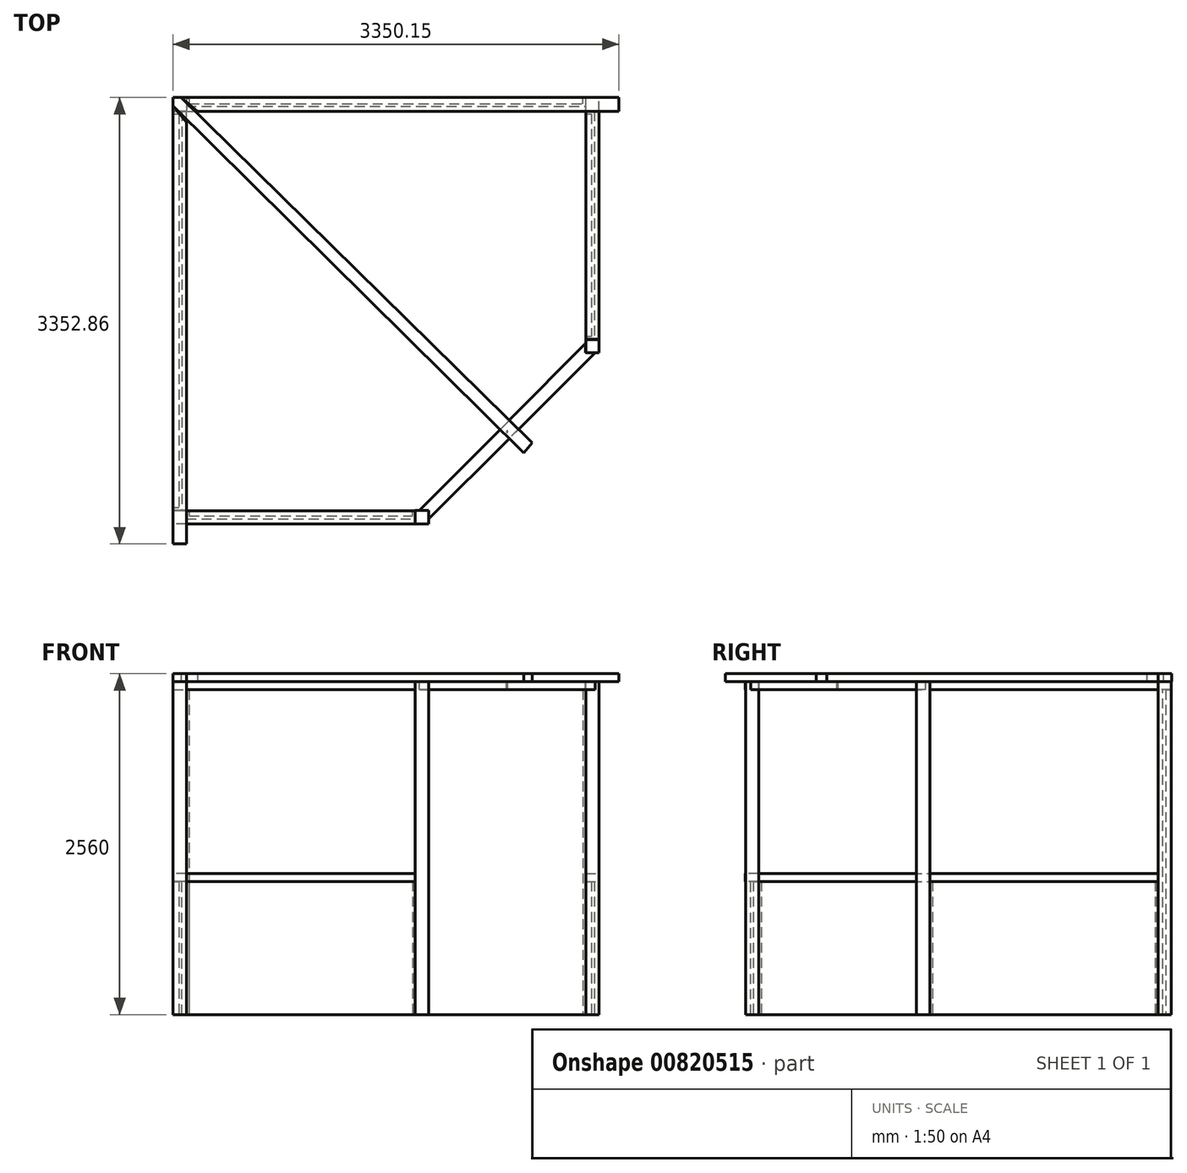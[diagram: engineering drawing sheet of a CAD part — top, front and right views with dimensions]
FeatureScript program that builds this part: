
annotation { "Feature Type Name" : "Feature", "Feature Type Description" : "" }
export const myFeature = defineFeature(function(context is Context, id is Id, definition is map)
    precondition{}
    {
        {
            var Q0;
            Q0=qCreatedBy(makeId("Top.planeOp"),FACE);
            var sketch = newSketch(context, id + "F0", { "sketchPlane" : qUnion([Q0])});
            skLineSegment(sketch, "E0.bottom", {"start": v(-213.47, 1424.3) * mm, "end": v(-113.47, 1424.3) * mm});
            skLineSegment(sketch, "E0.top", {"start": v(-213.47, 1324.3) * mm, "end": v(-113.47, 1324.3) * mm});
            skLineSegment(sketch, "E0.left", {"start": v(-213.47, 1424.3) * mm, "end": v(-213.47, 1324.3) * mm});
            skLineSegment(sketch, "E0.right", {"start": v(-113.47, 1424.3) * mm, "end": v(-113.47, 1324.3) * mm});
            skLineSegment(sketch, "E1.bottom", {"start": v(2886.53, 1324.3) * mm, "end": v(2986.53, 1324.3) * mm});
            skLineSegment(sketch, "E1.top", {"start": v(2886.53, 1424.3) * mm, "end": v(2986.53, 1424.3) * mm});
            skLineSegment(sketch, "E1.left", {"start": v(2886.53, 1324.3) * mm, "end": v(2886.53, 1424.3) * mm});
            skLineSegment(sketch, "E1.right", {"start": v(2986.53, 1324.3) * mm, "end": v(2986.53, 1424.3) * mm});
            skLineSegment(sketch, "E2.bottom", {"start": v(-113.47, -1675.7) * mm, "end": v(-213.47, -1675.7) * mm});
            skLineSegment(sketch, "E2.top", {"start": v(-113.47, -1775.7) * mm, "end": v(-213.47, -1775.7) * mm});
            skLineSegment(sketch, "E2.left", {"start": v(-113.47, -1675.7) * mm, "end": v(-113.47, -1775.7) * mm});
            skLineSegment(sketch, "E2.right", {"start": v(-213.47, -1675.7) * mm, "end": v(-213.47, -1775.7) * mm});
            skLineSegment(sketch, "E3.bottom", {"start": v(1606.53, -1675.7) * mm, "end": v(1706.53, -1675.7) * mm});
            skLineSegment(sketch, "E3.top", {"start": v(1606.53, -1775.7) * mm, "end": v(1706.53, -1775.7) * mm});
            skLineSegment(sketch, "E3.left", {"start": v(1606.53, -1675.7) * mm, "end": v(1606.53, -1775.7) * mm});
            skLineSegment(sketch, "E3.right", {"start": v(1706.53, -1675.7) * mm, "end": v(1706.53, -1775.7) * mm});
            skLineSegment(sketch, "E4.bottom", {"start": v(2886.53, -390.7) * mm, "end": v(2986.53, -390.7) * mm});
            skLineSegment(sketch, "E4.top", {"start": v(2886.53, -490.7) * mm, "end": v(2986.53, -490.7) * mm});
            skLineSegment(sketch, "E4.left", {"start": v(2886.53, -390.7) * mm, "end": v(2886.53, -490.7) * mm});
            skLineSegment(sketch, "E4.right", {"start": v(2986.53, -390.7) * mm, "end": v(2986.53, -490.7) * mm});
            skSolve(sketch);
        }
        {
            var Q0;
            Q0 = qSketchRegion(id + "F0", true);
            extrude(context, id + "F1", {"entities" : qUnion([Q0]), "depth" : 2500 * mm, "offsetDistance" : 25 * mm});
        }
        {
            var Q0;
            Q0=qCreatedBy(makeId("Top.planeOp"),FACE);
            var sketch = newSketch(context, id + "F2", { "sketchPlane" : qUnion([Q0])});
            skLineSegment(sketch, "E5.bottom", {"start": v(-113.6, 1421.35) * mm, "end": v(-93.6, 1421.35) * mm});
            skLineSegment(sketch, "E5.top", {"start": v(-113.6, 1381.35) * mm, "end": v(-93.6, 1381.35) * mm});
            skLineSegment(sketch, "E5.left", {"start": v(-113.6, 1421.35) * mm, "end": v(-113.6, 1381.35) * mm});
            skLineSegment(sketch, "E5.right", {"start": v(-93.6, 1421.35) * mm, "end": v(-93.6, 1381.35) * mm});
            skLineSegment(sketch, "E6.bottom", {"start": v(-113.6, 1381.35) * mm, "end": v(2886.4, 1381.35) * mm});
            skLineSegment(sketch, "E6.top", {"start": v(-113.6, 1360.35) * mm, "end": v(2886.4, 1360.35) * mm});
            skLineSegment(sketch, "E6.left", {"start": v(-113.6, 1381.35) * mm, "end": v(-113.6, 1360.35) * mm});
            skLineSegment(sketch, "E6.right", {"start": v(2886.4, 1381.35) * mm, "end": v(2886.4, 1360.35) * mm});
            skLineSegment(sketch, "E7.bottom", {"start": v(2886.4, 1381.35) * mm, "end": v(2866.4, 1381.35) * mm});
            skLineSegment(sketch, "E7.top", {"start": v(2886.4, 1421.35) * mm, "end": v(2866.4, 1421.35) * mm});
            skLineSegment(sketch, "E7.left", {"start": v(2886.4, 1381.35) * mm, "end": v(2886.4, 1421.35) * mm});
            skLineSegment(sketch, "E7.right", {"start": v(2866.4, 1381.35) * mm, "end": v(2866.4, 1421.35) * mm});
            skSolve(sketch);
        }
        {
            var Q0;
            Q0 = qSketchRegion(id + "F2", true);
            extrude(context, id + "F3", {"entities" : qUnion([Q0]), "operationType" : NewBodyOperationType.ADD, "depth" : 2440 * mm, "offsetDistance" : 25 * mm});
        }
        {
            var Q0;
            Q0=qCreatedBy(makeId("Top.planeOp"),FACE);
            var sketch = newSketch(context, id + "F4", { "sketchPlane" : qUnion([Q0])});
            skLineSegment(sketch, "E8.bottom", {"start": v(-209.79, 1323.87) * mm, "end": v(-169.79, 1323.87) * mm});
            skLineSegment(sketch, "E8.top", {"start": v(-209.79, 1303.87) * mm, "end": v(-169.79, 1303.87) * mm});
            skLineSegment(sketch, "E8.left", {"start": v(-209.79, 1323.87) * mm, "end": v(-209.79, 1303.87) * mm});
            skLineSegment(sketch, "E8.right", {"start": v(-169.79, 1323.87) * mm, "end": v(-169.79, 1303.87) * mm});
            skLineSegment(sketch, "E9.bottom", {"start": v(-169.79, 1323.87) * mm, "end": v(-148.79, 1323.87) * mm});
            skLineSegment(sketch, "E9.top", {"start": v(-169.79, -1676.13) * mm, "end": v(-148.79, -1676.13) * mm});
            skLineSegment(sketch, "E9.left", {"start": v(-169.79, 1323.87) * mm, "end": v(-169.79, -1676.13) * mm});
            skLineSegment(sketch, "E9.right", {"start": v(-148.79, 1323.87) * mm, "end": v(-148.79, -1676.13) * mm});
            skLineSegment(sketch, "E10.bottom", {"start": v(-169.79, -1676.13) * mm, "end": v(-209.79, -1676.13) * mm});
            skLineSegment(sketch, "E10.top", {"start": v(-169.79, -1656.13) * mm, "end": v(-209.79, -1656.13) * mm});
            skLineSegment(sketch, "E10.left", {"start": v(-169.79, -1676.13) * mm, "end": v(-169.79, -1656.13) * mm});
            skLineSegment(sketch, "E10.right", {"start": v(-209.79, -1676.13) * mm, "end": v(-209.79, -1656.13) * mm});
            skSolve(sketch);
        }
        {
            var Q0;
            Q0 = qSketchRegion(id + "F4", true);
            extrude(context, id + "F5", {"entities" : qUnion([Q0]), "operationType" : NewBodyOperationType.ADD, "depth" : 1000 * mm, "offsetDistance" : 25 * mm});
        }
        {
            var Q0;
            Q0=qCreatedBy(makeId("Top.planeOp"),FACE);
            var sketch = newSketch(context, id + "F6", { "sketchPlane" : qUnion([Q0])});
            skLineSegment(sketch, "E11.bottom", {"start": v(-113.7, -1676.3) * mm, "end": v(-93.7, -1676.3) * mm});
            skLineSegment(sketch, "E11.top", {"start": v(-113.7, -1716.3) * mm, "end": v(-93.7, -1716.3) * mm});
            skLineSegment(sketch, "E11.left", {"start": v(-113.7, -1676.3) * mm, "end": v(-113.7, -1716.3) * mm});
            skLineSegment(sketch, "E11.right", {"start": v(-93.7, -1676.3) * mm, "end": v(-93.7, -1716.3) * mm});
            skLineSegment(sketch, "E12.bottom", {"start": v(-113.7, -1716.3) * mm, "end": v(1606.3, -1716.3) * mm});
            skLineSegment(sketch, "E12.top", {"start": v(-113.7, -1737.3) * mm, "end": v(1606.3, -1737.3) * mm});
            skLineSegment(sketch, "E12.left", {"start": v(-113.7, -1716.3) * mm, "end": v(-113.7, -1737.3) * mm});
            skLineSegment(sketch, "E12.right", {"start": v(1606.3, -1716.3) * mm, "end": v(1606.3, -1737.3) * mm});
            skLineSegment(sketch, "E13.bottom", {"start": v(1606.3, -1716.3) * mm, "end": v(1586.3, -1716.3) * mm});
            skLineSegment(sketch, "E13.top", {"start": v(1606.3, -1676.3) * mm, "end": v(1586.3, -1676.3) * mm});
            skLineSegment(sketch, "E13.left", {"start": v(1606.3, -1716.3) * mm, "end": v(1606.3, -1676.3) * mm});
            skLineSegment(sketch, "E13.right", {"start": v(1586.3, -1716.3) * mm, "end": v(1586.3, -1676.3) * mm});
            skSolve(sketch);
        }
        {
            var Q0;
            Q0 = qSketchRegion(id + "F6", true);
            extrude(context, id + "F7", {"entities" : qUnion([Q0]), "operationType" : NewBodyOperationType.ADD, "depth" : 1000 * mm, "offsetDistance" : 25 * mm});
        }
        {
            var Q0;
            Q0=qCreatedBy(makeId("Top.planeOp"),FACE);
            var sketch = newSketch(context, id + "F8", { "sketchPlane" : qUnion([Q0])});
            skLineSegment(sketch, "E14.bottom", {"start": v(2889.5, 1324.2) * mm, "end": v(2929.5, 1324.2) * mm});
            skLineSegment(sketch, "E14.top", {"start": v(2889.5, 1304.2) * mm, "end": v(2929.5, 1304.2) * mm});
            skLineSegment(sketch, "E14.left", {"start": v(2889.5, 1324.2) * mm, "end": v(2889.5, 1304.2) * mm});
            skLineSegment(sketch, "E14.right", {"start": v(2929.5, 1324.2) * mm, "end": v(2929.5, 1304.2) * mm});
            skLineSegment(sketch, "E15.bottom", {"start": v(2929.5, 1324.2) * mm, "end": v(2950.5, 1324.2) * mm});
            skLineSegment(sketch, "E15.top", {"start": v(2929.5, -390.8) * mm, "end": v(2950.5, -390.8) * mm});
            skLineSegment(sketch, "E15.left", {"start": v(2929.5, 1324.2) * mm, "end": v(2929.5, -390.8) * mm});
            skLineSegment(sketch, "E15.right", {"start": v(2950.5, 1324.2) * mm, "end": v(2950.5, -390.8) * mm});
            skLineSegment(sketch, "E16.bottom", {"start": v(2929.5, -390.8) * mm, "end": v(2889.5, -390.8) * mm});
            skLineSegment(sketch, "E16.top", {"start": v(2929.5, -370.8) * mm, "end": v(2889.5, -370.8) * mm});
            skLineSegment(sketch, "E16.left", {"start": v(2929.5, -390.8) * mm, "end": v(2929.5, -370.8) * mm});
            skLineSegment(sketch, "E16.right", {"start": v(2889.5, -390.8) * mm, "end": v(2889.5, -370.8) * mm});
            skSolve(sketch);
        }
        {
            var Q0;
            Q0 = qSketchRegion(id + "F8", true);
            extrude(context, id + "F9", {"entities" : qUnion([Q0]), "operationType" : NewBodyOperationType.ADD, "depth" : 1000 * mm, "offsetDistance" : 25 * mm});
        }
        {
            var Q0;
            Q0=makeQuery(id+"F1.opExtrude","CAP_FACE",FACE,{"disambiguationData":[OSD([sQuery(id+"F0.wireOp",EDGE,"E0.bottom"),sQuery(id+"F0.wireOp",EDGE,"E0.top"),sQuery(id+"F0.wireOp",EDGE,"E0.left"),sQuery(id+"F0.wireOp",EDGE,"E0.right")])],"isStart":false});
            var sketch = newSketch(context, id + "F10", { "sketchPlane" : qUnion([Q0])});
            skLineSegment(sketch, "E17.bottom", {"start": v(-113.47, 1324.3) * mm, "end": v(2886.53, 1324.3) * mm});
            skLineSegment(sketch, "E17.top", {"start": v(-113.47, 1424.3) * mm, "end": v(2886.53, 1424.3) * mm});
            skLineSegment(sketch, "E17.left", {"start": v(-113.47, 1324.3) * mm, "end": v(-113.47, 1424.3) * mm});
            skLineSegment(sketch, "E17.right", {"start": v(2886.53, 1324.3) * mm, "end": v(2886.53, 1424.3) * mm});
            skLineSegment(sketch, "E18.bottom", {"start": v(-213.62, -1674.97) * mm, "end": v(-113.62, -1674.97) * mm});
            skLineSegment(sketch, "E18.top", {"start": v(-213.62, 1325.03) * mm, "end": v(-113.62, 1325.03) * mm});
            skLineSegment(sketch, "E18.left", {"start": v(-213.62, -1674.97) * mm, "end": v(-213.62, 1325.03) * mm});
            skLineSegment(sketch, "E18.right", {"start": v(-113.62, -1674.97) * mm, "end": v(-113.62, 1325.03) * mm});
            skLineSegment(sketch, "E19.bottom", {"start": v(-113.62, -1776.28) * mm, "end": v(1606.38, -1776.28) * mm});
            skLineSegment(sketch, "E19.top", {"start": v(-113.62, -1676.28) * mm, "end": v(1606.38, -1676.28) * mm});
            skLineSegment(sketch, "E19.left", {"start": v(-113.62, -1776.28) * mm, "end": v(-113.62, -1676.28) * mm});
            skLineSegment(sketch, "E19.right", {"start": v(1606.38, -1776.28) * mm, "end": v(1606.38, -1676.28) * mm});
            skLineSegment(sketch, "E20.bottom", {"start": v(2886.7, -389.73) * mm, "end": v(2986.7, -389.73) * mm});
            skLineSegment(sketch, "E20.top", {"start": v(2886.7, 1325.27) * mm, "end": v(2986.7, 1325.27) * mm});
            skLineSegment(sketch, "E20.left", {"start": v(2886.7, -389.73) * mm, "end": v(2886.7, 1325.27) * mm});
            skLineSegment(sketch, "E20.right", {"start": v(2986.7, -389.73) * mm, "end": v(2986.7, 1325.27) * mm});
            skLineSegment(sketch, "E21", {"start": v(1637.92, -1675.12) * mm, "end": v(2886.2, -420.23) * mm});
            skLineSegment(sketch, "E22", {"start": v(2886.2, -420.23) * mm, "end": v(2886.2, -420.23) * mm});
            skLineSegment(sketch, "E23", {"start": v(2886.2, -420.23) * mm, "end": v(2886.2, -491.07) * mm});
            skLineSegment(sketch, "E24", {"start": v(2886.2, -491.07) * mm, "end": v(2956.8, -491.07) * mm});
            skLineSegment(sketch, "E25", {"start": v(1706.94, -1736.4) * mm, "end": v(1706.94, -1675.12) * mm});
            skLineSegment(sketch, "E26", {"start": v(1706.94, -1675.12) * mm, "end": v(1637.92, -1675.12) * mm});
            skLineSegment(sketch, "E27", {"start": v(2956.8, -491.07) * mm, "end": v(1706.94, -1736.4) * mm});
            skSolve(sketch);
        }
        {
            var Q0;
            Q0 = qSketchRegion(id + "F10", true);
            extrude(context, id + "F11", {"entities" : qUnion([Q0]), "oppositeDirection" : true, "depth" : 60 * mm, "offsetDistance" : 25 * mm});
        }
        {
            var Q0;
            Q0=makeQuery(id+"F7.opExtrude","CAP_FACE",FACE,{"disambiguationData":[OSD([sQuery(id+"F6.wireOp",EDGE,"E11.bottom"),sQuery(id+"F6.wireOp",EDGE,"E11.left"),sQuery(id+"F6.wireOp",EDGE,"E11.right"),sQuery(id+"F6.wireOp",EDGE,"E12.bottom"),sQuery(id+"F6.wireOp",EDGE,"E12.top"),sQuery(id+"F6.wireOp",EDGE,"E12.left"),sQuery(id+"F6.wireOp",EDGE,"E12.right"),sQuery(id+"F6.wireOp",EDGE,"E13.top"),sQuery(id+"F6.wireOp",EDGE,"E13.left"),sQuery(id+"F6.wireOp",EDGE,"E13.right")])],"isStart":false});
            var sketch = newSketch(context, id + "F12", { "sketchPlane" : qUnion([Q0])});
            skLineSegment(sketch, "E28.bottom", {"start": v(-113.47, -1676.3) * mm, "end": v(1606.53, -1676.3) * mm});
            skLineSegment(sketch, "E28.top", {"start": v(-113.47, -1776.3) * mm, "end": v(1606.53, -1776.3) * mm});
            skLineSegment(sketch, "E28.left", {"start": v(-113.47, -1676.3) * mm, "end": v(-113.47, -1776.3) * mm});
            skLineSegment(sketch, "E28.right", {"start": v(1606.53, -1676.3) * mm, "end": v(1606.53, -1776.3) * mm});
            skLineSegment(sketch, "E29.bottom", {"start": v(-113.47, -1676.3) * mm, "end": v(-213.47, -1676.3) * mm});
            skLineSegment(sketch, "E29.top", {"start": v(-113.47, 1323.7) * mm, "end": v(-213.47, 1323.7) * mm});
            skLineSegment(sketch, "E29.left", {"start": v(-113.47, -1676.3) * mm, "end": v(-113.47, 1323.7) * mm});
            skLineSegment(sketch, "E29.right", {"start": v(-213.47, -1676.3) * mm, "end": v(-213.47, 1323.7) * mm});
            skLineSegment(sketch, "E30.bottom", {"start": v(2887.53, 1323.7) * mm, "end": v(2987.53, 1323.7) * mm});
            skLineSegment(sketch, "E30.top", {"start": v(2887.53, -391.3) * mm, "end": v(2987.53, -391.3) * mm});
            skLineSegment(sketch, "E30.left", {"start": v(2887.53, 1323.7) * mm, "end": v(2887.53, -391.3) * mm});
            skLineSegment(sketch, "E30.right", {"start": v(2987.53, 1323.7) * mm, "end": v(2987.53, -391.3) * mm});
            skSolve(sketch);
        }
        {
            var Q0;
            Q0 = qSketchRegion(id + "F12", true);
            extrude(context, id + "F13", {"entities" : qUnion([Q0]), "depth" : 60 * mm, "offsetDistance" : 25 * mm});
        }
        {
            var Q0;
            Q0=makeQuery(id+"F11.opExtrude","CAP_FACE",FACE,{"disambiguationData":[OSD([sQuery(id+"F10.wireOp",EDGE,"E18.bottom"),sQuery(id+"F10.wireOp",EDGE,"E18.top"),sQuery(id+"F10.wireOp",EDGE,"E18.left"),sQuery(id+"F10.wireOp",EDGE,"E18.right")])],"isStart":true});
            var sketch = newSketch(context, id + "F14", { "sketchPlane" : qUnion([Q0])});
            skLineSegment(sketch, "E31", {"start": v(-213.62, 1364.3) * mm, "end": v(-213.62, -1925.7) * mm});
            skLineSegment(sketch, "E32", {"start": v(-213.62, -1925.7) * mm, "end": v(-113.62, -1925.7) * mm});
            skLineSegment(sketch, "E33", {"start": v(-113.62, -1925.7) * mm, "end": v(-113.62, 1239.3) * mm});
            skLineSegment(sketch, "E34", {"start": v(-113.62, 1239.3) * mm, "end": v(-213.62, 1364.3) * mm});
            skLineSegment(sketch, "E35", {"start": v(-153.47, 1427.16) * mm, "end": v(3136.53, 1427.16) * mm});
            skLineSegment(sketch, "E36", {"start": v(3136.53, 1427.16) * mm, "end": v(3136.53, 1323.85) * mm});
            skLineSegment(sketch, "E37", {"start": v(3136.53, 1323.85) * mm, "end": v(-28.47, 1323.85) * mm});
            skLineSegment(sketch, "E38", {"start": v(-28.47, 1323.85) * mm, "end": v(-153.47, 1427.16) * mm});
            skLineSegment(sketch, "E39", {"start": v(-213.62, 1364.3) * mm, "end": v(-213.62, 1427.16) * mm});
            skLineSegment(sketch, "E40", {"start": v(-153.47, 1427.16) * mm, "end": v(2485.98, -1165.77) * mm});
            skLineSegment(sketch, "E41", {"start": v(2485.98, -1165.77) * mm, "end": v(2422.28, -1242.86) * mm});
            skLineSegment(sketch, "E42", {"start": v(2422.28, -1242.86) * mm, "end": v(-213.62, 1364.3) * mm});
            skLineSegment(sketch, "E43", {"start": v(-213.62, 1427.16) * mm, "end": v(-153.47, 1427.16) * mm});
            skSolve(sketch);
        }
        {
            var Q0;
            Q0=makeQuery(id+"F11.opExtrude","CAP_FACE",FACE,{"disambiguationData":[OSD([sQuery(id+"F10.wireOp",EDGE,"E21"),sQuery(id+"F10.wireOp",EDGE,"E23"),sQuery(id+"F10.wireOp",EDGE,"E24"),sQuery(id+"F10.wireOp",EDGE,"E25"),sQuery(id+"F10.wireOp",EDGE,"E26"),sQuery(id+"F10.wireOp",EDGE,"E27")])],"isStart":true});
            var sketch = newSketch(context, id + "F15", { "sketchPlane" : qUnion([Q0])});
            skCircle(sketch, "E44", {"center": v(2296.58, -1083.1) * mm, "radius": 5 * mm});
            skSolve(sketch);
        }
        {
            var Q0;
            Q0=makeQuery(id+"F15.imprint","IMPRINT",FACE,{"disambiguationData":[TD([[makeQuery(id+"F15.imprint","IMPRINT",EDGE,{"derivedFrom":sQuery(id+"F15.wireOp",EDGE,"E44")}),1.0]])]});
            var Q1;
            Q1=sQuery(id+"F15.wireOp",EDGE,"E44");
            extrude(context, id + "F16", {"entities" : qUnion([Q0]), "operationType" : NewBodyOperationType.REMOVE, "surfaceEntities" : qUnion([Q1]), "endBound" : BoundingType.THROUGH_ALL, "oppositeDirection" : true, "depth" : 25 * mm, "offsetDistance" : 25 * mm});
        }
        {
            var Q0;
            Q0 = qSketchRegion(id + "F14", true);
            extrude(context, id + "F17", {"entities" : qUnion([Q0]), "depth" : 60 * mm, "offsetDistance" : 25 * mm});
        }
    });
